# Revit family: m8crebf)
name_source: partatom
category: Plumbing Fixtures
units: mm (PartAtom-declared; Revit-internal decimal feet)

## family parameters
Always vertical = Yes
Cut with Voids When Loaded = No
OmniClass Number = 23.65.70.14.11
OmniClass Title = Drinking Fountains/Coolers
Part Type = Normal
Room Calculation Point = No
Round Connector Dimension = Use Diameter
Shared = No
Work Plane-Based = No

## types (1)
- Standard
    CW Connection = Yes
    Connector_3_Diameter = 0' - 0 1/4"
    Connector_4_Diameter = 0' - 0 1/4"
    Connector_5_Diameter = 0' - 1 1/4"
    Connector_6_Diameter = 0' - 5 1/2"
    Connector_7_Diameter = 0' - 5 1/2"
    Default Elevation = 0' - 0"
    Description = BI-LEVEL RADII FOUNTAIN W/ INTEGRATED ELECTRONIC BOTTLE FILLER, REFRIGERATED
    HW Connection = No
    Manufacturer = Oasis International
    Model = M8CREBF
    URL = https://www.oasiscoolers.com
    Vent Connection = No
    Waste Connection = Yes

## geometry (parser evidence)
native form markers: Sweep x3
no freeform markers — native parametric forms only
